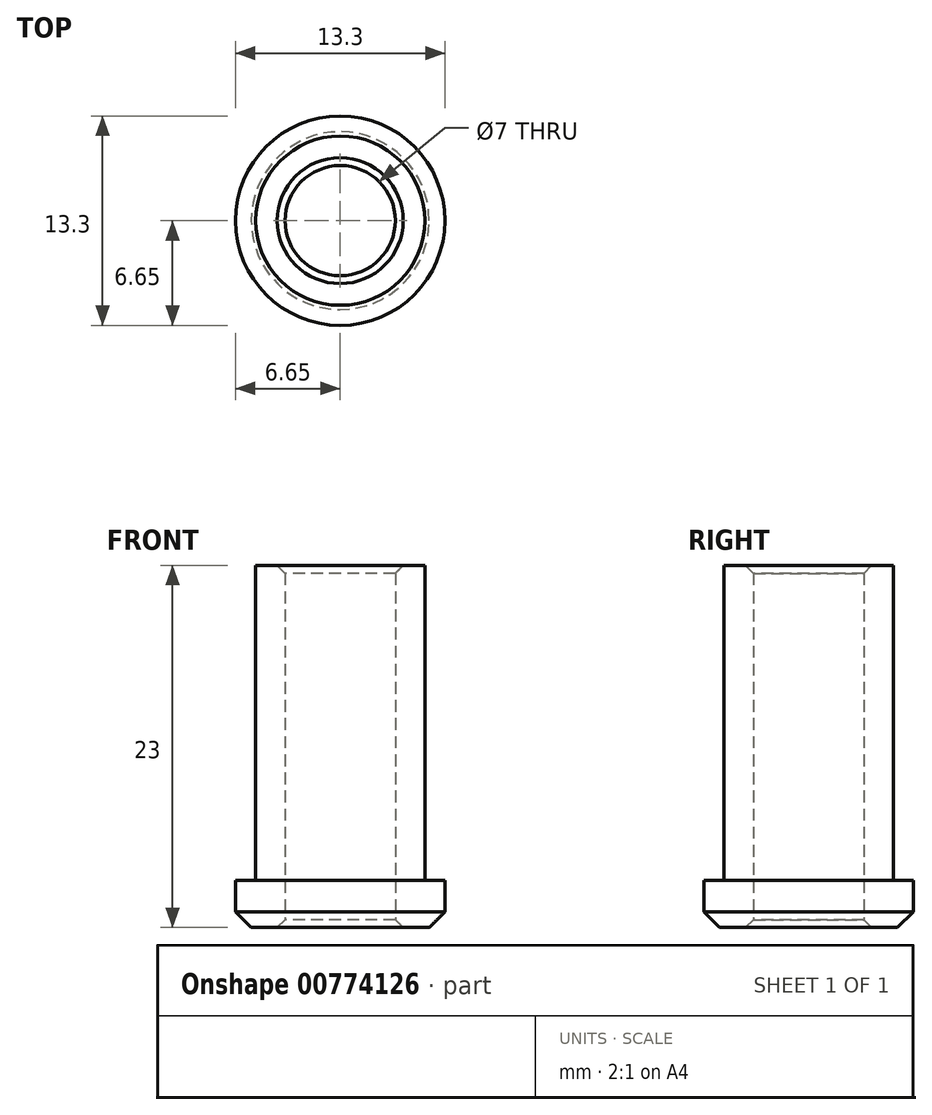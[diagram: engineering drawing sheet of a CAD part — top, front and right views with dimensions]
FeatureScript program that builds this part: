
annotation { "Feature Type Name" : "Feature", "Feature Type Description" : "" }
export const myFeature = defineFeature(function(context is Context, id is Id, definition is map)
    precondition{}
    {
        {
            var Q0;
            Q0=qCreatedBy(makeId("Top.planeOp"),FACE);
            var sketch = newSketch(context, id + "F0", { "sketchPlane" : qUnion([Q0])});
            skCircle(sketch, "E0", {"center": v(0, 0) * mm, "radius": 6.65 * mm});
            skCircle(sketch, "E1", {"center": v(0, 0) * mm, "radius": 3.5 * mm});
            skSolve(sketch);
        }
        {
            var Q0;
            Q0 = qSketchRegion(id + "F0", true);
            extrude(context, id + "F1", {"entities" : qUnion([Q0]), "depth" : 3 * mm, "offsetDistance" : 25 * mm});
        }
        {
            var Q0;
            Q0=makeQuery(id+"F1.opExtrude","CAP_FACE",FACE,{"disambiguationData":[OSD([sQuery(id+"F0.wireOp",EDGE,"E0"),sQuery(id+"F0.wireOp",EDGE,"E1")])],"isStart":false});
            var sketch = newSketch(context, id + "F2", { "sketchPlane" : qUnion([Q0])});
            skCircle(sketch, "E2", {"center": v(0, 0) * mm, "radius": 5.38 * mm});
            skCircle(sketch, "E3.0", {"center": v(0, 0) * mm, "radius": 3.5 * mm});
            skSolve(sketch);
        }
        {
            var Q0;
            Q0 = qSketchRegion(id + "F2", true);
            extrude(context, id + "F3", {"entities" : qUnion([Q0]), "operationType" : NewBodyOperationType.ADD, "depth" : 20 * mm, "offsetDistance" : 25 * mm});
        }
        {
            var Q0;
            Q0=makeQuery(id+"F1.opExtrude","CAP_EDGE",EDGE,{"disambiguationData":[OSD([sQuery(id+"F0.wireOp",EDGE,"E0")])],"isStart":true});
            chamfer(context, id + "F4", {"entities" : qUnion([Q0]), "width" : 1 * mm, "tangentPropagation" : true});
        }
        {
            var Q0;
            Q0=makeQuery(id+"F3.opExtrude","CAP_EDGE",EDGE,{"disambiguationData":[OSD([sQuery(id+"F2.wireOp",EDGE,"E3.0")])],"isStart":false});
            var Q1;
            Q1=makeQuery(id+"F1.opExtrude","CAP_EDGE",EDGE,{"disambiguationData":[OSD([sQuery(id+"F0.wireOp",EDGE,"E1")])],"isStart":true});
            chamfer(context, id + "F5", {"entities" : qUnion([Q0, Q1]), "width" : .5 * mm, "tangentPropagation" : true});
        }
    });
